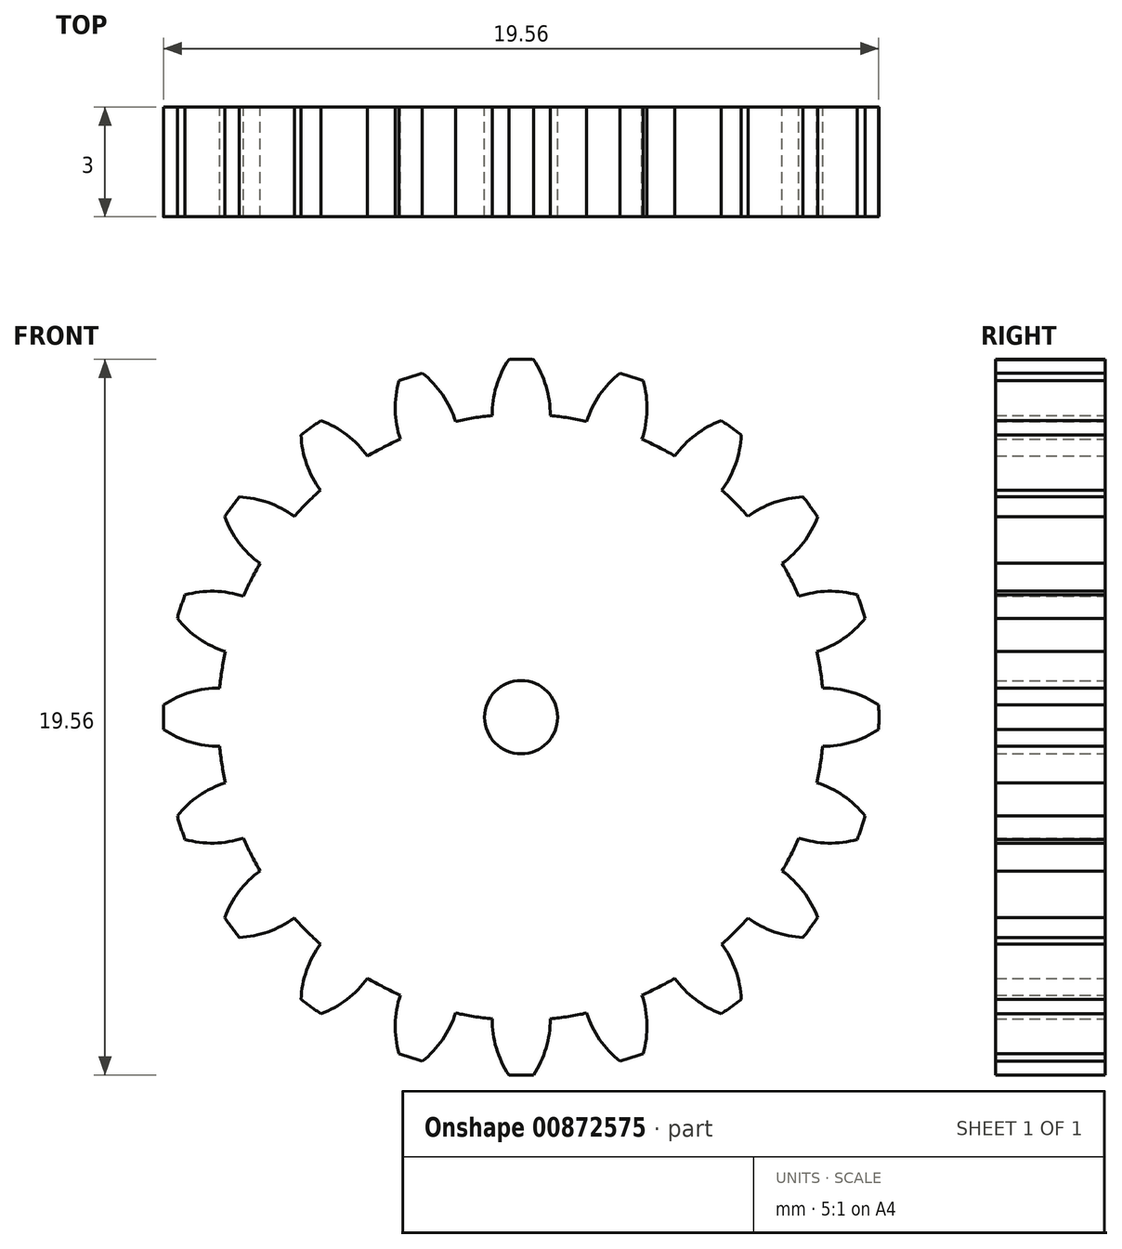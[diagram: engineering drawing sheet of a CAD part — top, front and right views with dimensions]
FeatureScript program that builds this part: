
annotation { "Feature Type Name" : "Feature", "Feature Type Description" : "" }
export const myFeature = defineFeature(function(context is Context, id is Id, definition is map)
    precondition{}
    {
        {
            var Q0;
            Q0=qCreatedBy(makeId("Front.planeOp"),FACE);
            var sketch = newSketch(context, id + "F0", { "sketchPlane" : qUnion([Q0])});
            skCircle(sketch, "E0", {"center": v(0, 0) * mm, "radius": 8.29 * mm});
            skArc(sketch, "E1", {"start": v(0.34, 9.78) * mm, "mid": v(0, 9.79) * mm, "end": v(-0.34, 9.78) * mm});
            skArc(sketch, "E2", {"start": v(-0.34, 9.78) * mm, "mid": v(-0.68, 9.05) * mm, "end": v(-0.8, 8.25) * mm});
            skArc(sketch, "E3.MirrorCS", {"start": v(0.34, 9.78) * mm, "mid": v(0.68, 9.05) * mm, "end": v(0.8, 8.25) * mm});
            skArc(sketch, "E4.1.0", {"start": v(-2.7, 9.4) * mm, "mid": v(-2.15, 8.81) * mm, "end": v(-1.8, 8.09) * mm});
            skArc(sketch, "E4.1.1", {"start": v(-2.7, 9.4) * mm, "mid": v(-3.02, 9.3) * mm, "end": v(-3.34, 9.2) * mm});
            skArc(sketch, "E4.1.2", {"start": v(-3.34, 9.2) * mm, "mid": v(-3.44, 8.4) * mm, "end": v(-3.3, 7.6) * mm});
            skArc(sketch, "E4.2.0", {"start": v(-5.48, 8.1) * mm, "mid": v(-4.77, 7.72) * mm, "end": v(-4.2, 7.14) * mm});
            skArc(sketch, "E4.2.1", {"start": v(-5.48, 8.1) * mm, "mid": v(-5.75, 7.92) * mm, "end": v(-6.02, 7.71) * mm});
            skArc(sketch, "E4.2.2", {"start": v(-6.02, 7.71) * mm, "mid": v(-5.87, 6.92) * mm, "end": v(-5.5, 6.2) * mm});
            skArc(sketch, "E4.3.0", {"start": v(-7.71, 6.02) * mm, "mid": v(-6.92, 5.87) * mm, "end": v(-6.2, 5.5) * mm});
            skArc(sketch, "E4.3.1", {"start": v(-7.71, 6.02) * mm, "mid": v(-7.92, 5.75) * mm, "end": v(-8.1, 5.48) * mm});
            skArc(sketch, "E4.3.2", {"start": v(-8.1, 5.48) * mm, "mid": v(-7.72, 4.77) * mm, "end": v(-7.14, 4.2) * mm});
            skArc(sketch, "E4.4.0", {"start": v(-9.2, 3.34) * mm, "mid": v(-8.4, 3.44) * mm, "end": v(-7.6, 3.3) * mm});
            skArc(sketch, "E4.4.1", {"start": v(-9.2, 3.34) * mm, "mid": v(-9.3, 3.02) * mm, "end": v(-9.4, 2.7) * mm});
            skArc(sketch, "E4.4.2", {"start": v(-9.4, 2.7) * mm, "mid": v(-8.81, 2.15) * mm, "end": v(-8.09, 1.8) * mm});
            skArc(sketch, "E4.5.0", {"start": v(-9.78, 0.34) * mm, "mid": v(-9.05, 0.68) * mm, "end": v(-8.25, 0.8) * mm});
            skArc(sketch, "E4.5.1", {"start": v(-9.78, 0.34) * mm, "mid": v(-9.79, 0) * mm, "end": v(-9.78, -0.34) * mm});
            skArc(sketch, "E4.5.2", {"start": v(-9.78, -0.34) * mm, "mid": v(-9.05, -0.68) * mm, "end": v(-8.25, -0.8) * mm});
            skArc(sketch, "E4.6.0", {"start": v(-9.4, -2.7) * mm, "mid": v(-8.81, -2.15) * mm, "end": v(-8.09, -1.8) * mm});
            skArc(sketch, "E4.6.1", {"start": v(-9.4, -2.7) * mm, "mid": v(-9.3, -3.02) * mm, "end": v(-9.2, -3.34) * mm});
            skArc(sketch, "E4.6.2", {"start": v(-9.2, -3.34) * mm, "mid": v(-8.4, -3.44) * mm, "end": v(-7.6, -3.3) * mm});
            skArc(sketch, "E4.7.0", {"start": v(-8.1, -5.48) * mm, "mid": v(-7.72, -4.77) * mm, "end": v(-7.14, -4.2) * mm});
            skArc(sketch, "E4.7.1", {"start": v(-8.1, -5.48) * mm, "mid": v(-7.92, -5.75) * mm, "end": v(-7.71, -6.02) * mm});
            skArc(sketch, "E4.7.2", {"start": v(-7.71, -6.02) * mm, "mid": v(-6.92, -5.87) * mm, "end": v(-6.2, -5.5) * mm});
            skArc(sketch, "E4.8.0", {"start": v(-6.02, -7.71) * mm, "mid": v(-5.87, -6.92) * mm, "end": v(-5.5, -6.2) * mm});
            skArc(sketch, "E4.8.1", {"start": v(-6.02, -7.71) * mm, "mid": v(-5.75, -7.92) * mm, "end": v(-5.48, -8.1) * mm});
            skArc(sketch, "E4.8.2", {"start": v(-5.48, -8.1) * mm, "mid": v(-4.77, -7.72) * mm, "end": v(-4.2, -7.14) * mm});
            skArc(sketch, "E5.1.9.0", {"start": v(-3.34, -9.2) * mm, "mid": v(-3.44, -8.4) * mm, "end": v(-3.3, -7.6) * mm});
            skArc(sketch, "E5.4.9.0", {"start": v(-3.34, -9.2) * mm, "mid": v(-3.02, -9.3) * mm, "end": v(-2.7, -9.4) * mm});
            skArc(sketch, "E5.8.9.0", {"start": v(-2.7, -9.4) * mm, "mid": v(-2.15, -8.81) * mm, "end": v(-1.8, -8.09) * mm});
            skArc(sketch, "E5.1.10.0", {"start": v(-0.34, -9.78) * mm, "mid": v(-0.68, -9.05) * mm, "end": v(-0.8, -8.25) * mm});
            skArc(sketch, "E5.4.10.0", {"start": v(-0.34, -9.78) * mm, "mid": v(0, -9.79) * mm, "end": v(0.34, -9.78) * mm});
            skArc(sketch, "E5.8.10.0", {"start": v(0.34, -9.78) * mm, "mid": v(0.68, -9.05) * mm, "end": v(0.8, -8.25) * mm});
            skArc(sketch, "E5.1.11.0", {"start": v(2.7, -9.4) * mm, "mid": v(2.15, -8.81) * mm, "end": v(1.8, -8.09) * mm});
            skArc(sketch, "E5.4.11.0", {"start": v(2.7, -9.4) * mm, "mid": v(3.02, -9.3) * mm, "end": v(3.34, -9.2) * mm});
            skArc(sketch, "E5.8.11.0", {"start": v(3.34, -9.2) * mm, "mid": v(3.44, -8.4) * mm, "end": v(3.3, -7.6) * mm});
            skArc(sketch, "E5.1.12.0", {"start": v(5.48, -8.1) * mm, "mid": v(4.77, -7.72) * mm, "end": v(4.2, -7.14) * mm});
            skArc(sketch, "E5.4.12.0", {"start": v(5.48, -8.1) * mm, "mid": v(5.75, -7.92) * mm, "end": v(6.02, -7.71) * mm});
            skArc(sketch, "E5.8.12.0", {"start": v(6.02, -7.71) * mm, "mid": v(5.87, -6.92) * mm, "end": v(5.5, -6.2) * mm});
            skArc(sketch, "E5.1.13.0", {"start": v(7.71, -6.02) * mm, "mid": v(6.92, -5.87) * mm, "end": v(6.2, -5.5) * mm});
            skArc(sketch, "E5.4.13.0", {"start": v(7.71, -6.02) * mm, "mid": v(7.92, -5.75) * mm, "end": v(8.1, -5.48) * mm});
            skArc(sketch, "E5.8.13.0", {"start": v(8.1, -5.48) * mm, "mid": v(7.72, -4.77) * mm, "end": v(7.14, -4.2) * mm});
            skArc(sketch, "E5.1.14.0", {"start": v(9.2, -3.34) * mm, "mid": v(8.4, -3.44) * mm, "end": v(7.6, -3.3) * mm});
            skArc(sketch, "E5.4.14.0", {"start": v(9.2, -3.34) * mm, "mid": v(9.3, -3.02) * mm, "end": v(9.4, -2.7) * mm});
            skArc(sketch, "E5.8.14.0", {"start": v(9.4, -2.7) * mm, "mid": v(8.81, -2.15) * mm, "end": v(8.09, -1.8) * mm});
            skArc(sketch, "E5.1.15.0", {"start": v(9.78, -0.34) * mm, "mid": v(9.05, -0.68) * mm, "end": v(8.25, -0.8) * mm});
            skArc(sketch, "E5.4.15.0", {"start": v(9.78, -0.34) * mm, "mid": v(9.79, 0) * mm, "end": v(9.78, 0.34) * mm});
            skArc(sketch, "E5.8.15.0", {"start": v(9.78, 0.34) * mm, "mid": v(9.05, 0.68) * mm, "end": v(8.25, 0.8) * mm});
            skArc(sketch, "E5.1.16.0", {"start": v(9.4, 2.7) * mm, "mid": v(8.81, 2.15) * mm, "end": v(8.09, 1.8) * mm});
            skArc(sketch, "E5.4.16.0", {"start": v(9.4, 2.7) * mm, "mid": v(9.3, 3.02) * mm, "end": v(9.2, 3.34) * mm});
            skArc(sketch, "E5.8.16.0", {"start": v(9.2, 3.34) * mm, "mid": v(8.4, 3.44) * mm, "end": v(7.6, 3.3) * mm});
            skArc(sketch, "E5.1.17.0", {"start": v(8.1, 5.48) * mm, "mid": v(7.72, 4.77) * mm, "end": v(7.14, 4.2) * mm});
            skArc(sketch, "E5.4.17.0", {"start": v(8.1, 5.48) * mm, "mid": v(7.92, 5.75) * mm, "end": v(7.71, 6.02) * mm});
            skArc(sketch, "E5.8.17.0", {"start": v(7.71, 6.02) * mm, "mid": v(6.92, 5.87) * mm, "end": v(6.2, 5.5) * mm});
            skArc(sketch, "E6.1.18.0", {"start": v(6.02, 7.71) * mm, "mid": v(5.87, 6.92) * mm, "end": v(5.5, 6.2) * mm});
            skArc(sketch, "E6.4.18.0", {"start": v(6.02, 7.71) * mm, "mid": v(5.75, 7.92) * mm, "end": v(5.48, 8.1) * mm});
            skArc(sketch, "E6.8.18.0", {"start": v(5.48, 8.1) * mm, "mid": v(4.77, 7.72) * mm, "end": v(4.2, 7.14) * mm});
            skArc(sketch, "E7.1.19.0", {"start": v(3.34, 9.2) * mm, "mid": v(3.44, 8.4) * mm, "end": v(3.3, 7.6) * mm});
            skArc(sketch, "E7.4.19.0", {"start": v(3.34, 9.2) * mm, "mid": v(3.02, 9.3) * mm, "end": v(2.7, 9.4) * mm});
            skArc(sketch, "E7.8.19.0", {"start": v(2.7, 9.4) * mm, "mid": v(2.15, 8.81) * mm, "end": v(1.8, 8.09) * mm});
            skSolve(sketch);
        }
        {
            var Q0;
            Q0=qSketchRegion(id+"F0",true);
            extrude(context, id + "F1", {"entities" : qUnion([Q0]), "depth" : 3 * mm, "offsetDistance" : 25 * mm});
        }
        {
            var Q0;
            Q0=makeQuery(id+"F1.opExtrude","CAP_FACE",FACE,{"disambiguationData":[OSD([sQuery(id+"F0.wireOp",EDGE,"E0"),sQuery(id+"F0.wireOp",EDGE,"E1"),sQuery(id+"F0.wireOp",EDGE,"E2"),sQuery(id+"F0.wireOp",EDGE,"E3.MirrorCS"),sQuery(id+"F0.wireOp",EDGE,"E4.1.0"),sQuery(id+"F0.wireOp",EDGE,"E4.1.1"),sQuery(id+"F0.wireOp",EDGE,"E4.1.2"),sQuery(id+"F0.wireOp",EDGE,"E4.2.0"),sQuery(id+"F0.wireOp",EDGE,"E4.2.1"),sQuery(id+"F0.wireOp",EDGE,"E4.2.2"),sQuery(id+"F0.wireOp",EDGE,"E4.3.0"),sQuery(id+"F0.wireOp",EDGE,"E4.3.1"),sQuery(id+"F0.wireOp",EDGE,"E4.3.2"),sQuery(id+"F0.wireOp",EDGE,"E4.4.0"),sQuery(id+"F0.wireOp",EDGE,"E4.4.1"),sQuery(id+"F0.wireOp",EDGE,"E4.4.2"),sQuery(id+"F0.wireOp",EDGE,"E4.5.0"),sQuery(id+"F0.wireOp",EDGE,"E4.5.1"),sQuery(id+"F0.wireOp",EDGE,"E4.5.2"),sQuery(id+"F0.wireOp",EDGE,"E4.6.0"),sQuery(id+"F0.wireOp",EDGE,"E4.6.1"),sQuery(id+"F0.wireOp",EDGE,"E4.6.2"),sQuery(id+"F0.wireOp",EDGE,"E4.7.0"),sQuery(id+"F0.wireOp",EDGE,"E4.7.1"),sQuery(id+"F0.wireOp",EDGE,"E4.7.2"),sQuery(id+"F0.wireOp",EDGE,"E4.8.0"),sQuery(id+"F0.wireOp",EDGE,"E4.8.1"),sQuery(id+"F0.wireOp",EDGE,"E4.8.2")])],"isStart":true});
            var sketch = newSketch(context, id + "F2", { "sketchPlane" : qUnion([Q0])});
            skCircle(sketch, "E8", {"center": v(0, 0) * mm, "radius": 1 * mm});
            skSolve(sketch);
        }
        {
            var Q0;
            Q0=makeQuery(id+"F2.imprint","IMPRINT",FACE,{"disambiguationData":[TD([[makeQuery(id+"F2.imprint","IMPRINT",EDGE,{"derivedFrom":sQuery(id+"F2.wireOp",EDGE,"E8")}),1.0]])]});
            extrude(context, id + "F3", {"entities" : qUnion([Q0]), "operationType" : NewBodyOperationType.REMOVE, "endBound" : BoundingType.THROUGH_ALL, "oppositeDirection" : true, "depth" : 25 * mm, "offsetDistance" : 25 * mm});
        }
        {
            var Q0;
            Q0=makeQuery(id+"F1.opExtrude","SWEPT_BODY",BODY,{"disambiguationData":[OSD([sQuery(id+"F0.wireOp",EDGE,"E0"),sQuery(id+"F0.wireOp",EDGE,"E1"),sQuery(id+"F0.wireOp",EDGE,"E2"),sQuery(id+"F0.wireOp",EDGE,"E3.MirrorCS"),sQuery(id+"F0.wireOp",EDGE,"E4.1.0"),sQuery(id+"F0.wireOp",EDGE,"E4.1.1"),sQuery(id+"F0.wireOp",EDGE,"E4.1.2"),sQuery(id+"F0.wireOp",EDGE,"E4.2.0"),sQuery(id+"F0.wireOp",EDGE,"E4.2.1"),sQuery(id+"F0.wireOp",EDGE,"E4.2.2"),sQuery(id+"F0.wireOp",EDGE,"E4.3.0"),sQuery(id+"F0.wireOp",EDGE,"E4.3.1"),sQuery(id+"F0.wireOp",EDGE,"E4.3.2"),sQuery(id+"F0.wireOp",EDGE,"E4.4.0"),sQuery(id+"F0.wireOp",EDGE,"E4.4.1"),sQuery(id+"F0.wireOp",EDGE,"E4.4.2"),sQuery(id+"F0.wireOp",EDGE,"E4.5.0"),sQuery(id+"F0.wireOp",EDGE,"E4.5.1"),sQuery(id+"F0.wireOp",EDGE,"E4.5.2"),sQuery(id+"F0.wireOp",EDGE,"E4.6.0"),sQuery(id+"F0.wireOp",EDGE,"E4.6.1"),sQuery(id+"F0.wireOp",EDGE,"E4.6.2"),sQuery(id+"F0.wireOp",EDGE,"E4.7.0"),sQuery(id+"F0.wireOp",EDGE,"E4.7.1"),sQuery(id+"F0.wireOp",EDGE,"E4.7.2"),sQuery(id+"F0.wireOp",EDGE,"E4.8.0"),sQuery(id+"F0.wireOp",EDGE,"E4.8.1"),sQuery(id+"F0.wireOp",EDGE,"E4.8.2")])]});
            transform(context, id + "F4", {"entities" : qUnion([Q0]), "transformType" : TransformType.TRANSLATION_3D, "dx" : 0 * mm, "dy" : 0 * mm, "dz" : 0 * mm, "makeCopy" : true});
        }
        {
            var Q0;
            Q0=makeQuery(id+"F4.opPattern","COPY",BODY,{"derivedFrom":makeQuery(id+"F1.opExtrude","SWEPT_BODY",BODY,{"disambiguationData":[OSD([sQuery(id+"F0.wireOp",EDGE,"E0"),sQuery(id+"F0.wireOp",EDGE,"E1"),sQuery(id+"F0.wireOp",EDGE,"E2"),sQuery(id+"F0.wireOp",EDGE,"E3.MirrorCS"),sQuery(id+"F0.wireOp",EDGE,"E4.1.0"),sQuery(id+"F0.wireOp",EDGE,"E4.1.1"),sQuery(id+"F0.wireOp",EDGE,"E4.1.2"),sQuery(id+"F0.wireOp",EDGE,"E4.2.0"),sQuery(id+"F0.wireOp",EDGE,"E4.2.1"),sQuery(id+"F0.wireOp",EDGE,"E4.2.2"),sQuery(id+"F0.wireOp",EDGE,"E4.3.0"),sQuery(id+"F0.wireOp",EDGE,"E4.3.1"),sQuery(id+"F0.wireOp",EDGE,"E4.3.2"),sQuery(id+"F0.wireOp",EDGE,"E4.4.0"),sQuery(id+"F0.wireOp",EDGE,"E4.4.1"),sQuery(id+"F0.wireOp",EDGE,"E4.4.2"),sQuery(id+"F0.wireOp",EDGE,"E4.5.0"),sQuery(id+"F0.wireOp",EDGE,"E4.5.1"),sQuery(id+"F0.wireOp",EDGE,"E4.5.2"),sQuery(id+"F0.wireOp",EDGE,"E4.6.0"),sQuery(id+"F0.wireOp",EDGE,"E4.6.1"),sQuery(id+"F0.wireOp",EDGE,"E4.6.2"),sQuery(id+"F0.wireOp",EDGE,"E4.7.0"),sQuery(id+"F0.wireOp",EDGE,"E4.7.1"),sQuery(id+"F0.wireOp",EDGE,"E4.7.2"),sQuery(id+"F0.wireOp",EDGE,"E4.8.0"),sQuery(id+"F0.wireOp",EDGE,"E4.8.1"),sQuery(id+"F0.wireOp",EDGE,"E4.8.2")])]}),"instanceName":"1"});
            deleteBodies(context, id + "F5", {"entities" : qUnion([Q0])});
        }
    });
